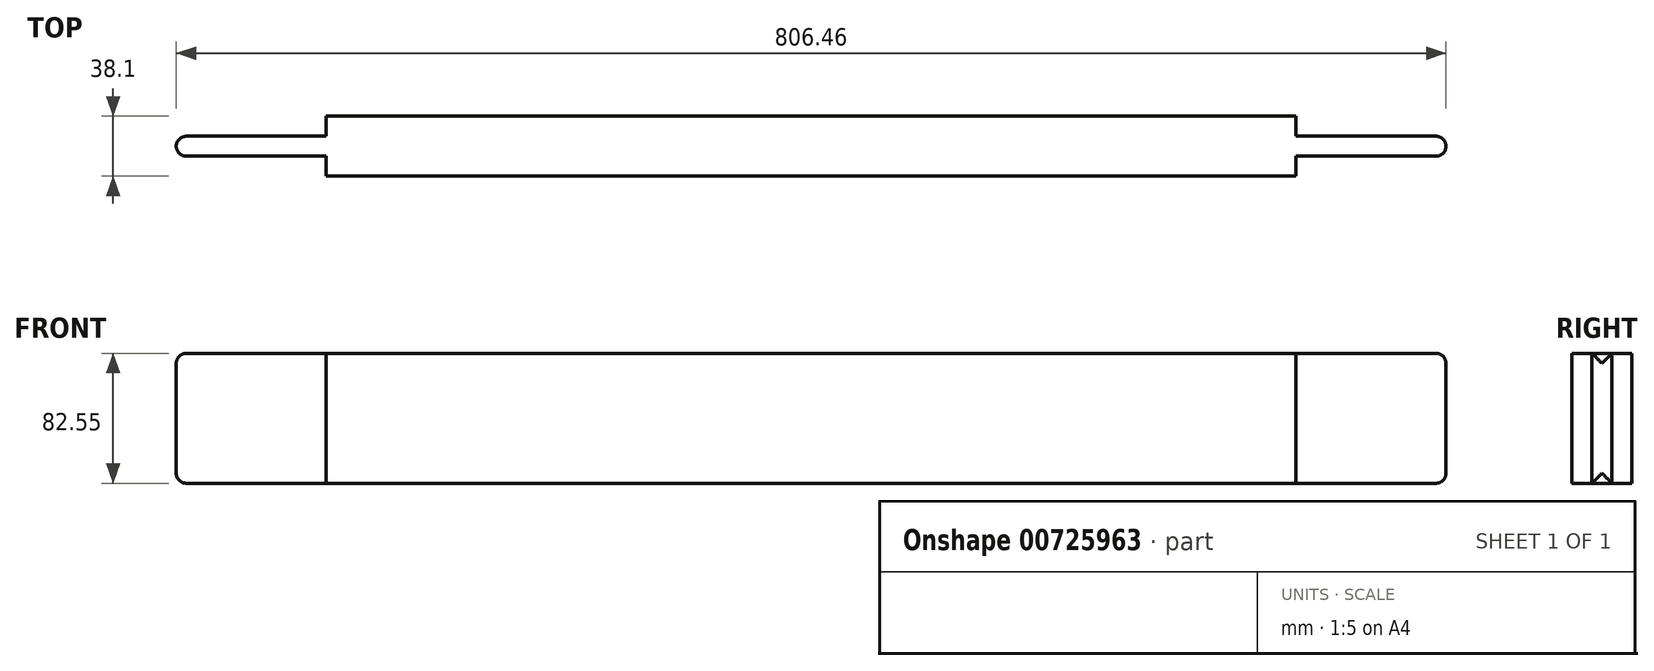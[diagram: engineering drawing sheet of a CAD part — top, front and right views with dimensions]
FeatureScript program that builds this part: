
annotation { "Feature Type Name" : "Feature", "Feature Type Description" : "" }
export const myFeature = defineFeature(function(context is Context, id is Id, definition is map)
    precondition{}
    {
        {
            var Q0;
            Q0=qCreatedBy(makeId("Top.planeOp"),FACE);
            var sketch = newSketch(context, id + "F0", { "sketchPlane" : qUnion([Q0])});
            skLineSegment(sketch, "E0.bottom", {"start": v(-307.98, -19.05) * mm, "end": v(307.98, -19.05) * mm});
            skLineSegment(sketch, "E0.top", {"start": v(-307.98, 19.05) * mm, "end": v(307.98, 19.05) * mm});
            skLineSegment(sketch, "E0.left", {"start": v(-307.98, -19.05) * mm, "end": v(-307.98, 19.05) * mm});
            skLineSegment(sketch, "E0.right", {"start": v(307.98, -19.05) * mm, "end": v(307.98, 19.05) * mm});
            skPoint(sketch, "E0.middle", {"position": v(0, 0) * mm});
            skLineSegment(sketch, "E1.bottom", {"start": v(-307.98, -6.35) * mm, "end": v(-403.23, -6.35) * mm});
            skLineSegment(sketch, "E1.top", {"start": v(-307.98, 6.35) * mm, "end": v(-403.23, 6.35) * mm});
            skLineSegment(sketch, "E1.left", {"start": v(-307.98, -6.35) * mm, "end": v(-307.98, 6.35) * mm});
            skLineSegment(sketch, "E1.right", {"start": v(-403.23, -6.35) * mm, "end": v(-403.23, 6.35) * mm});
            skPoint(sketch, "E1.middle", {"position": v(-355.6, 0) * mm});
            skLineSegment(sketch, "E2.bottom", {"start": v(307.98, -6.35) * mm, "end": v(403.22, -6.35) * mm});
            skLineSegment(sketch, "E2.top", {"start": v(307.98, 6.35) * mm, "end": v(403.22, 6.35) * mm});
            skLineSegment(sketch, "E2.left", {"start": v(307.98, -6.35) * mm, "end": v(307.98, 6.35) * mm});
            skLineSegment(sketch, "E2.right", {"start": v(403.23, -6.35) * mm, "end": v(403.23, 6.35) * mm});
            skPoint(sketch, "E2.middle", {"position": v(355.6, 0) * mm});
            skSolve(sketch);
        }
        {
            var Q0;
            {var subQ3=sQuery(id+"F0.wireOp",EDGE,"E0.bottom");Q0=makeQuery(id+"F0.imprint","IMPRINT",FACE,{"disambiguationData":[TD([[makeQuery(id+"F0.imprint","IMPRINT",EDGE,{"derivedFrom":subQ3}),1.0]])]});}
            var Q1;
            Q1=makeQuery(id+"F0.imprint","IMPRINT",FACE,{"disambiguationData":[TD([[makeQuery(id+"F0.imprint","IMPRINT",EDGE,{"derivedFrom":sQuery(id+"F0.wireOp",EDGE,"E1.bottom")}),-1.0]])]});
            var Q2;
            Q2=makeQuery(id+"F0.imprint","IMPRINT",FACE,{"disambiguationData":[TD([[makeQuery(id+"F0.imprint","IMPRINT",EDGE,{"derivedFrom":sQuery(id+"F0.wireOp",EDGE,"E2.bottom")}),1.0]])]});
            extrude(context, id + "F1", {"entities" : qUnion([Q0, Q1, Q2]), "depth" : 82.55 * mm, "offsetDistance" : 25.4 * mm});
        }
        {
            var Q0;
            Q0=makeQuery(id+"F1.opExtrude","SWEPT_EDGE",EDGE,{"disambiguationData":[OSD([sQuery(id+"F0.wireOp",EDGE,"E1.bottom"),sQuery(id+"F0.wireOp",EDGE,"E1.right")])]});
            var Q1;
            Q1=makeQuery(id+"F1.opExtrude","SWEPT_EDGE",EDGE,{"disambiguationData":[OSD([sQuery(id+"F0.wireOp",EDGE,"E1.top"),sQuery(id+"F0.wireOp",EDGE,"E1.right")])]});
            var Q2;
            Q2=makeQuery(id+"F1.opExtrude","SWEPT_EDGE",EDGE,{"disambiguationData":[OSD([sQuery(id+"F0.wireOp",EDGE,"E2.bottom"),sQuery(id+"F0.wireOp",EDGE,"E2.right")])]});
            var Q3;
            Q3=makeQuery(id+"F1.opExtrude","SWEPT_EDGE",EDGE,{"disambiguationData":[OSD([sQuery(id+"F0.wireOp",EDGE,"E2.top"),sQuery(id+"F0.wireOp",EDGE,"E2.right")])]});
            var Q4;
            Q4=makeQuery(id+"F1.opExtrude","CAP_EDGE",EDGE,{"disambiguationData":[OSD([sQuery(id+"F0.wireOp",EDGE,"E2.right")])],"isStart":false});
            var Q5;
            Q5=makeQuery(id+"F1.opExtrude","CAP_EDGE",EDGE,{"disambiguationData":[OSD([sQuery(id+"F0.wireOp",EDGE,"E2.right")])],"isStart":true});
            var Q6;
            Q6=makeQuery(id+"F1.opExtrude","CAP_EDGE",EDGE,{"disambiguationData":[OSD([sQuery(id+"F0.wireOp",EDGE,"E1.right")])],"isStart":true});
            var Q7;
            Q7=makeQuery(id+"F1.opExtrude","CAP_EDGE",EDGE,{"disambiguationData":[OSD([sQuery(id+"F0.wireOp",EDGE,"E1.right")])],"isStart":false});
            fillet(context, id + "F2", {"entities" : qUnion([Q0, Q1, Q2, Q3, Q4, Q5, Q6, Q7]), "radius" : 6.35 * mm, "tangentPropagation" : true, "allowEdgeOverflow" : false});
        }
    });
